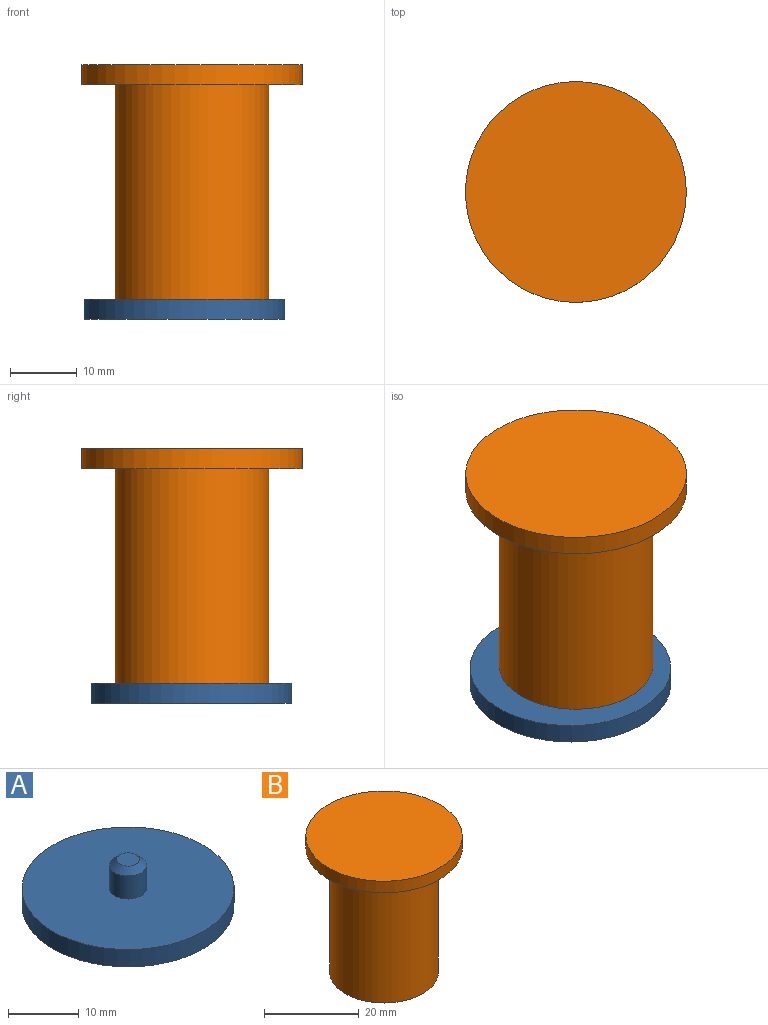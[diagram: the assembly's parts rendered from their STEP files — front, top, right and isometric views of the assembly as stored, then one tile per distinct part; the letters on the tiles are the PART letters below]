
ASSEMBLY  parts=2 mates=1
PART A: 6 faces, bbox 30x30x8 mm
  f0: cylinder r=15mm len=30mm, axis (0,0,-1), area 282.7mm2, adj f1,f2
  f1: plane 30x30mm, normal (0,0,1), area 685.2mm2, adj f0,f3
  f2: plane 30x30mm, normal (0,0,-1), area 706.9mm2, adj f0
  f3: cylinder r=2.62mm len=5.25mm, axis (0,0,-1), area 66mm2, adj f1,f5
  f4: plane 3.25x3.25mm, normal (0,0,1), area 8.3mm2, adj f5
  f5: cone r=1.62mm half-angle=45deg, axis (0,0,-1), area 18.9mm2, adj f3,f4
PART B: 10 faces, bbox 33.6x33.6x36.4 mm
  f0: cylinder r=3mm len=6mm, axis (0,0,-1), area 26.1mm2, adj f2,f6,f7,f8,f9
  f1: cylinder r=11.5mm len=32mm, axis (0,0,-1), area 2312.2mm2, adj f2,f5
  f2: plane 23.59x23.59mm, normal (0,0,-1), area 383.7mm2, adj f0,f1,f7,f8
  f3: cylinder r=16.5mm len=33mm, axis (0,0,-1), area 311mm2, adj f4,f5
  f4: plane 33x33mm, normal (0,0,1), area 855.3mm2, adj f3
  f5: plane 33x33mm, normal (0,0,-1), area 439.8mm2, adj f1,f3
  f6: plane 6x6mm, normal (0,0,-1), area 28.3mm2, adj f0
  f7: bspline ~7.97x6.9mm, area 38.5mm2, adj f0,f2,f8,f9
  f8: bspline ~7.97x6.9mm, area 83.9mm2, adj f0,f2,f7,f9
  f9: plane 0.78x0.45mm, normal (0,-1,0), area 0.2mm2, adj f0,f7,f8
PLACE A t=(-1.12,0.06,-9.59)mm
PLACE B t=(0,0,-6.59)mm
MATE planar A.f0 <-> B.f2  axis (0,0,1) through (-1.12,0.06,-6.59)mm
